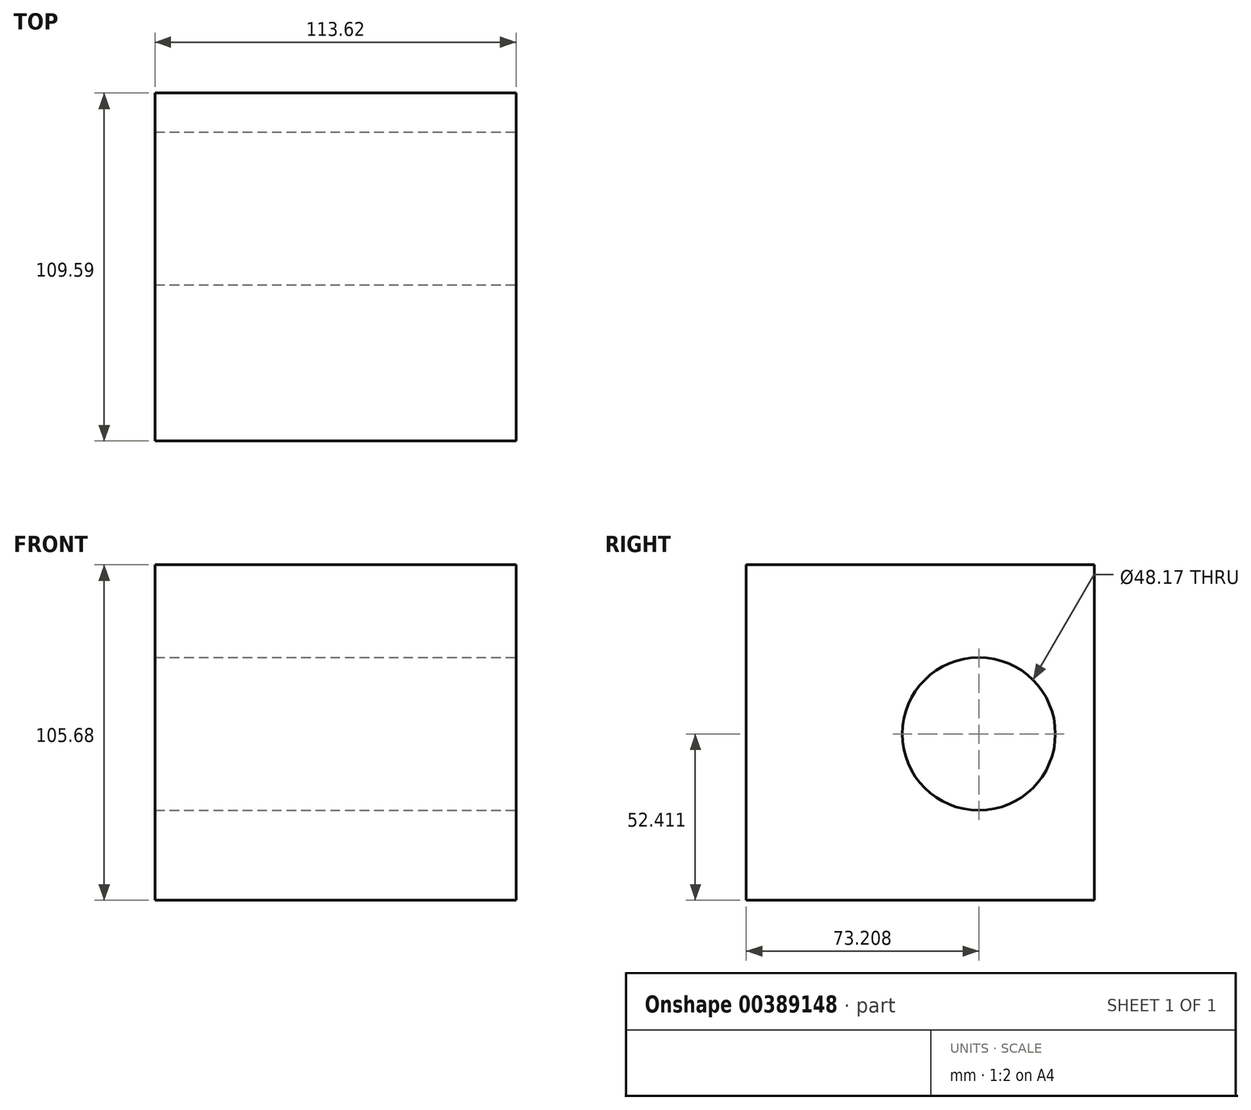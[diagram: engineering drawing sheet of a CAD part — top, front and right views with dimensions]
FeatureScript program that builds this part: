
annotation { "Feature Type Name" : "Feature", "Feature Type Description" : "" }
export const myFeature = defineFeature(function(context is Context, id is Id, definition is map)
    precondition{}
    {
        {
            var Q0;
            Q0=qCreatedBy(makeId("Top.planeOp"),FACE);
            var sketch = newSketch(context, id + "F0", { "sketchPlane" : qUnion([Q0])});
            skLineSegment(sketch, "E0.bottom", {"start": v(-60.63, 74.43) * mm, "end": v(52.99, 74.43) * mm});
            skLineSegment(sketch, "E0.top", {"start": v(-60.63, -35.16) * mm, "end": v(52.99, -35.16) * mm});
            skLineSegment(sketch, "E0.left", {"start": v(-60.63, 74.43) * mm, "end": v(-60.63, -35.16) * mm});
            skLineSegment(sketch, "E0.right", {"start": v(52.99, 74.43) * mm, "end": v(52.99, -35.16) * mm});
            skSolve(sketch);
        }
        {
            var Q0;
            Q0=makeQuery(id+"F0.imprint","IMPRINT",FACE,{"disambiguationData":[TD([[makeQuery(id+"F0.imprint","IMPRINT",EDGE,{"derivedFrom":sQuery(id+"F0.wireOp",EDGE,"E0.bottom")}),-1.0]])]});
            extrude(context, id + "F1", {"entities" : qUnion([Q0]), "depth" : 105.68 * mm, "hasDraft" : true, "draftAngle" : 0 * degree});
        }
        {
            var Q0;
            Q0=makeQuery(id+"F1.opExtrude","SWEPT_FACE",FACE,{"disambiguationData":[OSD([sQuery(id+"F0.wireOp",EDGE,"E0.right")])]});
            var sketch = newSketch(context, id + "F2", { "sketchPlane" : qUnion([Q0])});
            skCircle(sketch, "E1", {"center": v(38.05, 52.41) * mm, "radius": 24.08 * mm});
            skSolve(sketch);
        }
        {
            var Q0;
            Q0 = qSketchRegion(id + "F2", true);
            extrude(context, id + "F3", {"entities" : qUnion([Q0]), "operationType" : NewBodyOperationType.REMOVE, "oppositeDirection" : true, "depth" : 200 * mm});
        }
        {
            var Q0;
            Q0=qCreatedBy(makeId("Right.planeOp"),FACE);
            var sketch = newSketch(context, id + "F4", { "sketchPlane" : qUnion([Q0])});
            skFitSpline(sketch, "E2", {"points": [v(-93.42, 47.9) * mm, v(-12.57, 90.3) * mm, v(94.84, 63.7) * mm], "startDerivative": vector(161.5, 122.34) * mm, "endDerivative": vector(214.18, -87.38) * mm});
            skSolve(sketch);
        }
        {
            var Q0;
            Q0 = qSketchRegion(id + "F4", true);
            var Q1;
            Q1 = qBodyType(qCreatedBy(id + "F4" ,EDGE), BodyType.WIRE);
            var Q2;
            Q2=makeQuery(id+"F1.opExtrude","CAP_EDGE",EDGE,{"disambiguationData":[OSD([sQuery(id+"F0.wireOp",EDGE,"E0.right")])],"isStart":true});
            revolve(context, id + "F5", {"bodyType" : ToolBodyType.SURFACE, "entities" : qUnion([Q0]), "surfaceEntities" : qUnion([Q1]), "axis" : qUnion([Q2]), "revolveType" : RevolveType.FULL});
        }
    });
